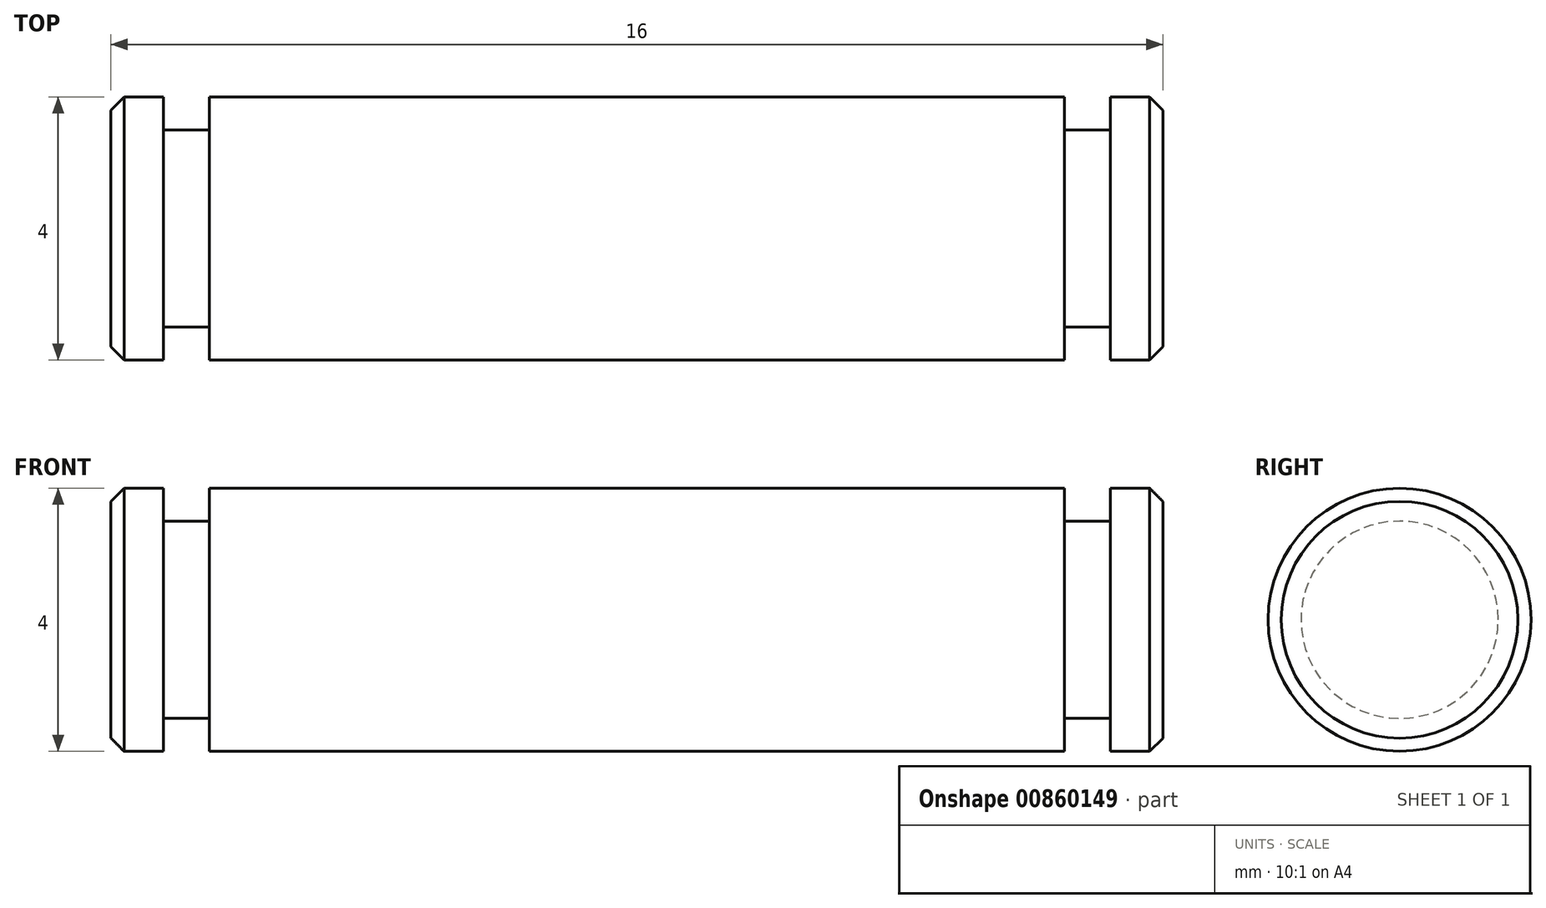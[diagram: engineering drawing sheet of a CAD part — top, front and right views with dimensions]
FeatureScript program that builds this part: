
annotation { "Feature Type Name" : "Feature", "Feature Type Description" : "" }
export const myFeature = defineFeature(function(context is Context, id is Id, definition is map)
    precondition{}
    {
        {
            var Q0;
            Q0=qCreatedBy(makeId("Front.planeOp"),FACE);
            var sketch = newSketch(context, id + "F0", { "sketchPlane" : qUnion([Q0])});
            skLineSegment(sketch, "E0", {"start": v(0, 0) * mm, "end": v(0, 2) * mm});
            skLineSegment(sketch, "E1", {"start": v(0, 2) * mm, "end": v(0.8, 2) * mm});
            skLineSegment(sketch, "E2", {"start": v(0.8, 2) * mm, "end": v(0.8, 1.5) * mm});
            skLineSegment(sketch, "E3", {"start": v(0.8, 1.5) * mm, "end": v(1.5, 1.5) * mm});
            skLineSegment(sketch, "E4", {"start": v(1.5, 1.5) * mm, "end": v(1.5, 2) * mm});
            skLineSegment(sketch, "E5", {"start": v(1.5, 2) * mm, "end": v(14.5, 2) * mm});
            skLineSegment(sketch, "E6", {"start": v(14.5, 2) * mm, "end": v(14.5, 1.5) * mm});
            skLineSegment(sketch, "E7", {"start": v(14.5, 1.5) * mm, "end": v(15.2, 1.5) * mm});
            skLineSegment(sketch, "E8", {"start": v(15.2, 1.5) * mm, "end": v(15.2, 2) * mm});
            skLineSegment(sketch, "E9", {"start": v(15.2, 2) * mm, "end": v(16, 2) * mm});
            skLineSegment(sketch, "E10", {"start": v(16, 2) * mm, "end": v(16, 0) * mm});
            skLineSegment(sketch, "E11", {"start": v(16, 0) * mm, "end": v(0, 0) * mm});
            skSolve(sketch);
        }
        {
            var Q0;
            Q0=makeQuery(id+"F0.imprint","IMPRINT",FACE,{"disambiguationData":[TD([[makeQuery(id+"F0.imprint","IMPRINT",EDGE,{"derivedFrom":sQuery(id+"F0.wireOp",EDGE,"E0")}),-1.0]])]});
            var Q1;
            Q1=sQuery(id+"F0.wireOp",EDGE,"E11");
            revolve(context, id + "F1", {"surfaceOperationType" : NewSurfaceOperationType.NEW, "entities" : qUnion([Q0]), "axis" : qUnion([Q1]), "revolveType" : RevolveType.FULL});
        }
        {
            var Q0;
            Q0=makeQuery(id+"F1.opRevolve","SWEPT_EDGE",EDGE,{"disambiguationData":[OSD([sQuery(id+"F0.wireOp",EDGE,"E0"),sQuery(id+"F0.wireOp",EDGE,"E1")])]});
            var Q1;
            Q1=makeQuery(id+"F1.opRevolve","SWEPT_EDGE",EDGE,{"disambiguationData":[OSD([sQuery(id+"F0.wireOp",EDGE,"E9"),sQuery(id+"F0.wireOp",EDGE,"E10")])]});
            chamfer(context, id + "F2", {"entities" : qUnion([Q0, Q1]), "width" : 0.2 * mm, "tangentPropagation" : true});
        }
    });
